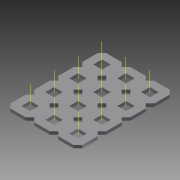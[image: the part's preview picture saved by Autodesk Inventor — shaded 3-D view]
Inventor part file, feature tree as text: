
AUTODESK INVENTOR PART (.ipt)
format: ipt  version: 2015 (Build 190159000, 159)  size: 1,118,208 bytes
history: native  units: in
note: dims shown in document units (in); Inventor stores cm internally (conversion verified against a paired STEP export)
features: other x21, extrude x2, pattern_linear x1, imported_body x1
ambient origin geometry x8: Origin, YZ Plane, XZ Plane, XY Plane, X Axis, Y Axis, Z Axis, Center Point
bodies: Body1 (feature_tree)
feature tree (25):
  other  "Diamond-Pattern"
  other  "Plate"
  extrude  "length cut"  TaperAngle=0.0deg  [1 undecoded]
  extrude  "width cut"  TaperAngle=0.0deg  [1 undecoded]
  other  "constraint axis"
  pattern_linear  "constraint axes"  Spacing1=0.5in  [1 undecoded]
  other  "front plane"
  other  "right plane"
  imported_body  "Base1"
  other  "length profile"
  other  "width profile"
  other  "Work Point1"
  other  "Work Axis36"
  other  "Work Axis37"
  other  "Work Axis38"
  other  "Work Axis40"
  other  "Work Axis41"
  other  "Work Axis42"
  other  "Work Axis43"
  other  "Work Axis44"
  other  "Work Axis45"
  other  "Work Axis46"
  other  "Work Axis47"
  other  "back plane"
  other  "left plane"
note: 3 required parameter values undecoded (feature->parameter linkage not recoverable at this tier; creation-order binding heuristic only, values carry confidence <= 0.55)
